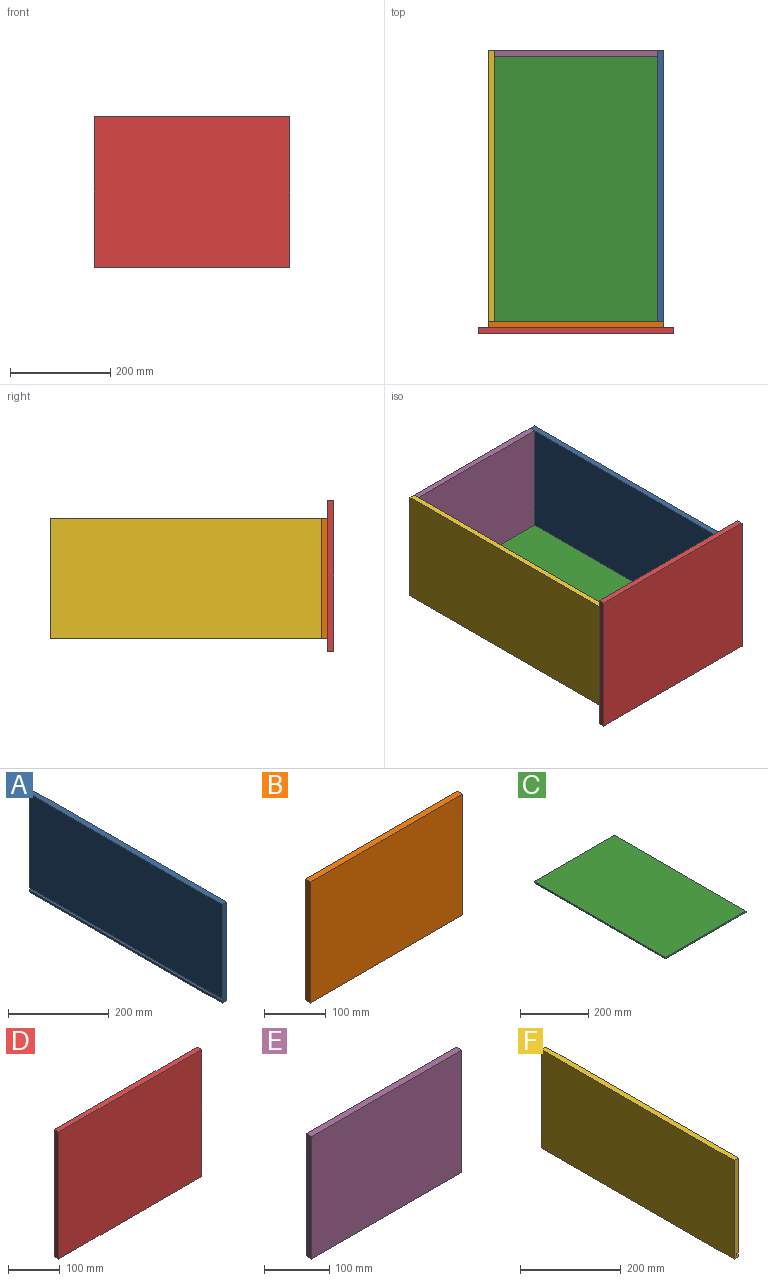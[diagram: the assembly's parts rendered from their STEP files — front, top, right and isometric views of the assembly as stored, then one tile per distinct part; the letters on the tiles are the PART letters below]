
ASSEMBLY  parts=6 mates=5
PART A: 10 faces, bbox 12x541x240 mm
  f0: plane 541x12mm, normal (0,0,-1), area 6492mm2, adj f1,f7,f8,f9
  f1: plane 541x5mm, normal (-1,0,0), area 2705mm2, adj f0,f2,f8,f9
  f2: plane 541x4mm, normal (0,0,1), area 2164mm2, adj f1,f3,f8,f9
  f3: plane 541x5mm, normal (-1,0,0), area 2705mm2, adj f2,f4,f8,f9
  f4: plane 541x4mm, normal (0,0,-1), area 2164mm2, adj f3,f5,f8,f9
  f5: plane 541x230mm, normal (-1,0,0), area 124430mm2, adj f4,f6,f8,f9
  f6: plane 541x12mm, normal (0,0,1), area 6492mm2, adj f5,f7,f8,f9
  f7: plane 541x240mm, normal (1,0,0), area 129840mm2, adj f0,f6,f8,f9
  f8: plane 240x12mm, normal (0,1,0), area 2860mm2, adj f0,f1,f2,f3,f4,f5,f6,f7
  f9: plane 240x12mm, normal (0,-1,0), area 2860mm2, adj f0,f1,f2,f3,f4,f5,f6,f7
PART B: 11 faces, bbox 350x12x240 mm
  f0: plane 350x240mm, normal (0,1,0), area 82330mm2, adj f1,f2,f3,f4,f6,f7,f8,f9
  f1: plane 240x12mm, normal (1,0,0), area 2880mm2, adj f0,f2,f4,f5
  f2: plane 350x12mm, normal (0,0,1), area 4200mm2, adj f0,f1,f3,f5
  f3: plane 240x12mm, normal (-1,0,0), area 2880mm2, adj f0,f2,f4,f5
  f4: plane 350x12mm, normal (0,0,-1), area 4200mm2, adj f0,f1,f3,f5
  f5: plane 350x240mm, normal (0,-1,0), area 84000mm2, adj f1,f2,f3,f4
  f6: plane 334x5mm, normal (0,0,1), area 1670mm2, adj f0,f7,f9,f10
  f7: plane 5x5mm, normal (1,0,0), area 25mm2, adj f0,f6,f8,f10
  f8: plane 334x5mm, normal (0,0,-1), area 1670mm2, adj f0,f7,f9,f10
  f9: plane 5x5mm, normal (-1,0,0), area 25mm2, adj f0,f6,f8,f10
  f10: plane 334x5mm, normal (0,1,0), area 1670mm2, adj f6,f7,f8,f9
PART C: 6 faces, bbox 334x546x5 mm
  f0: plane 334x5mm, normal (0,-1,0), area 1670mm2, adj f1,f3,f4,f5
  f1: plane 546x5mm, normal (-1,0,0), area 2730mm2, adj f0,f2,f4,f5
  f2: plane 334x5mm, normal (0,1,0), area 1670mm2, adj f1,f3,f4,f5
  f3: plane 546x5mm, normal (1,0,0), area 2730mm2, adj f0,f2,f4,f5
  f4: plane 546x334mm, normal (0,0,-1), area 182364mm2, adj f0,f1,f2,f3
  f5: plane 546x334mm, normal (0,0,1), area 182364mm2, adj f0,f1,f2,f3
PART D: 6 faces, bbox 390x12x300 mm
  f0: plane 300x12mm, normal (1,0,0), area 3600mm2, adj f1,f3,f4,f5
  f1: plane 390x12mm, normal (0,0,1), area 4680mm2, adj f0,f2,f4,f5
  f2: plane 300x12mm, normal (-1,0,0), area 3600mm2, adj f1,f3,f4,f5
  f3: plane 390x12mm, normal (0,0,-1), area 4680mm2, adj f0,f2,f4,f5
  f4: plane 390x300mm, normal (0,-1,0), area 117000mm2, adj f0,f1,f2,f3
  f5: plane 390x300mm, normal (0,1,0), area 117000mm2, adj f0,f1,f2,f3
PART E: 6 faces, bbox 326x12x230 mm
  f0: plane 326x12mm, normal (0,0,-1), area 3912mm2, adj f1,f3,f4,f5
  f1: plane 230x12mm, normal (-1,0,0), area 2760mm2, adj f0,f2,f4,f5
  f2: plane 326x12mm, normal (0,0,1), area 3912mm2, adj f1,f3,f4,f5
  f3: plane 230x12mm, normal (1,0,0), area 2760mm2, adj f0,f2,f4,f5
  f4: plane 326x230mm, normal (0,-1,0), area 74980mm2, adj f0,f1,f2,f3
  f5: plane 326x230mm, normal (0,1,0), area 74980mm2, adj f0,f1,f2,f3
PART F: 10 faces, bbox 12x541x240 mm
  f0: plane 541x4mm, normal (0,0,1), area 2164mm2, adj f1,f7,f8,f9
  f1: plane 541x5mm, normal (1,0,0), area 2705mm2, adj f0,f2,f8,f9
  f2: plane 541x12mm, normal (0,0,-1), area 6492mm2, adj f1,f3,f8,f9
  f3: plane 541x240mm, normal (-1,0,0), area 129840mm2, adj f2,f4,f8,f9
  f4: plane 541x12mm, normal (0,0,1), area 6492mm2, adj f3,f5,f8,f9
  f5: plane 541x230mm, normal (1,0,0), area 124430mm2, adj f4,f6,f8,f9
  f6: plane 541x4mm, normal (0,0,-1), area 2164mm2, adj f5,f7,f8,f9
  f7: plane 541x5mm, normal (1,0,0), area 2705mm2, adj f0,f6,f8,f9
  f8: plane 240x12mm, normal (0,1,0), area 2860mm2, adj f0,f1,f2,f3,f4,f5,f6,f7
  f9: plane 240x12mm, normal (0,-1,0), area 2860mm2, adj f0,f1,f2,f3,f4,f5,f6,f7
PLACE A t=(0,0,-125)mm
PLACE B t=(0,0,-125)mm fixed
PLACE C t=(0,0,-125)mm
PLACE D t=(0,0,-130)mm
PLACE E t=(0,0,-125)mm
PLACE F t=(0,0,-125)mm
MATE fastened E.f3 <-> A.f5  axis (1,0,0) through (163,553,135)mm
MATE fastened B.f5 <-> D.f5  axis (0,-1,0) through (0,0,15)mm
MATE fastened B.f10 <-> C.f0  axis (0,1,0) through (-167,7,-95)mm
MATE fastened B.f0 <-> A.f9  axis (0,1,0) through (175,12,-105)mm
MATE fastened B.f0 <-> F.f9  axis (0,1,0) through (175,12,-105)mm
